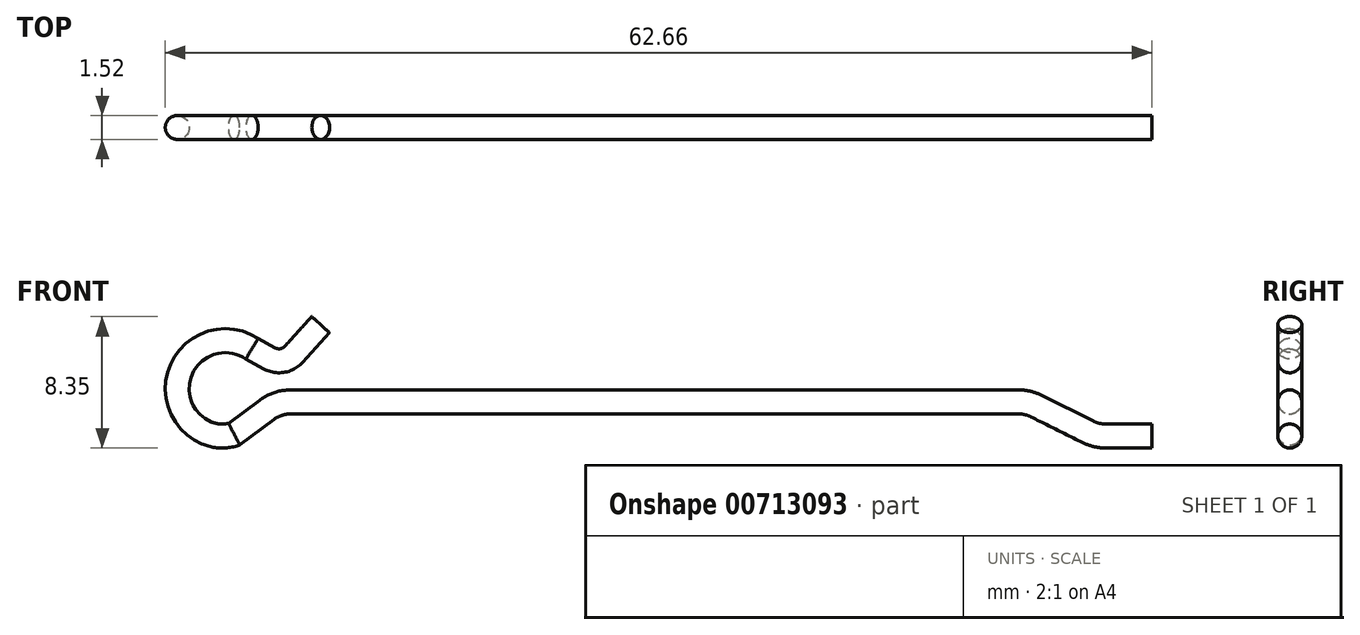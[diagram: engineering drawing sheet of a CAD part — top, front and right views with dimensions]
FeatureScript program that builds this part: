
annotation { "Feature Type Name" : "Feature", "Feature Type Description" : "" }
export const myFeature = defineFeature(function(context is Context, id is Id, definition is map)
    precondition{}
    {
        {
            var Q0;
            Q0=qCreatedBy(makeId("Front.planeOp"),FACE);
            var sketch = newSketch(context, id + "F0", { "sketchPlane" : qUnion([Q0])});
            skLineSegment(sketch, "E0", {"start": v(0, 0) * mm, "end": v(-2.93, 0) * mm});
            skLineSegment(sketch, "E1", {"start": v(-7.34, 1.9) * mm, "end": v(-4.07, 0.27) * mm});
            skLineSegment(sketch, "E2", {"start": v(-8.47, 2.17) * mm, "end": v(-54.7, 2.17) * mm});
            skLineSegment(sketch, "E3", {"start": v(-57.16, 5.54) * mm, "end": v(-56.04, 4.93) * mm});
            skPoint(sketch, "E4.visualSharp", {"position": v(-53.6, 2.17) * mm});
            skPoint(sketch, "E5.visualSharp", {"position": v(-7.87, 2.17) * mm});
            skArc(sketch, "E5.filletArc", {"start": v(-7.34, 1.9) * mm, "mid": v(-7.89, 2.1) * mm, "end": v(-8.47, 2.17) * mm});
            skPoint(sketch, "E6.visualSharp", {"position": v(-3.53, 0) * mm});
            skArc(sketch, "E6.filletArc", {"start": v(-4.07, 0.27) * mm, "mid": v(-3.51, 0.07) * mm, "end": v(-2.93, 0) * mm});
            skArc(sketch, "E7", {"start": v(-57.16, 5.54) * mm, "mid": v(-61.53, 4.46) * mm, "end": v(-60.04, 0.2) * mm});
            skPoint(sketch, "E8", {"position": v(-61.9, 3) * mm});
            skLineSegment(sketch, "E9", {"start": v(-59.64, 2.13) * mm, "end": v(-57.16, 5.54) * mm, "construction": true});
            skPoint(sketch, "E10.visualSharp", {"position": v(-58.16, 0.04) * mm});
            skArc(sketch, "E10.filletArc", {"start": v(-60.04, 0.2) * mm, "mid": v(-59.17, 0) * mm, "end": v(-58.28, 0.12) * mm});
            skLineSegment(sketch, "E11", {"start": v(-54.5, 5.2) * mm, "end": v(-52.79, 7.08) * mm});
            skLineSegment(sketch, "E12", {"start": v(-58.28, 0.12) * mm, "end": v(-58.78, 0.78) * mm});
            skLineSegment(sketch, "E13", {"start": v(-56.2, 1.66) * mm, "end": v(-58.28, 0.12) * mm});
            skPoint(sketch, "E14", {"position": v(-59.05, 0) * mm});
            skPoint(sketch, "E15.visualSharp", {"position": v(-55.53, 2.17) * mm});
            skArc(sketch, "E15.filletArc", {"start": v(-54.7, 2.17) * mm, "mid": v(-55.5, 2.04) * mm, "end": v(-56.2, 1.66) * mm});
            skPoint(sketch, "E16.visualSharp", {"position": v(-55.16, 4.46) * mm});
            skArc(sketch, "E16.filletArc", {"start": v(-56.04, 4.93) * mm, "mid": v(-55.22, 4.8) * mm, "end": v(-54.5, 5.2) * mm});
            skLineSegment(sketch, "E17", {"start": v(-54.5, 5.2) * mm, "end": v(-55.65, 7.4) * mm, "construction": true});
            skSolve(sketch);
        }
        {
            var Q0;
            Q0=sQuery(id+"F0.wireOp",VERTEX,"E0.start");
            var Q1;
            Q1=qCreatedBy(makeId("Right.planeOp"),FACE);
            cPlane(context, id + "F1", {"entities" : qUnion([Q0, Q1]), "cplaneType" : CPlaneType.PLANE_POINT, "offset" : 25.4 * mm, "width" : 152.4 * mm, "height" : 152.4 * mm});
        }
        {
            var Q0;
            Q0=qCreatedBy(id+"F1.planeOp",FACE);
            var sketch = newSketch(context, id + "F2", { "sketchPlane" : qUnion([Q0])});
            skCircle(sketch, "E18", {"center": v(0, 0) * mm, "radius": 0.76 * mm});
            skSolve(sketch);
        }
        {
            var Q0;
            Q0=makeQuery(id+"F2.imprint","IMPRINT",FACE,{"disambiguationData":[TD([[makeQuery(id+"F2.imprint","IMPRINT",EDGE,{"derivedFrom":sQuery(id+"F2.wireOp",EDGE,"E18")}),1.0]])]});
            var Q1;
            Q1=sQuery(id+"F0.wireOp",EDGE,"E0");
            var Q2;
            Q2=sQuery(id+"F0.wireOp",EDGE,"E6.filletArc");
            var Q3;
            Q3=sQuery(id+"F0.wireOp",EDGE,"E1");
            var Q4;
            Q4=sQuery(id+"F0.wireOp",EDGE,"E5.filletArc");
            var Q5;
            Q5=sQuery(id+"F0.wireOp",EDGE,"E2");
            var Q6;
            Q6=sQuery(id+"F0.wireOp",EDGE,"E15.filletArc");
            var Q7;
            Q7=sQuery(id+"F0.wireOp",EDGE,"E16.filletArc");
            var Q8;
            Q8=sQuery(id+"F0.wireOp",EDGE,"E11");
            var Q9;
            Q9=sQuery(id+"F0.wireOp",EDGE,"E3");
            var Q10;
            Q10=sQuery(id+"F0.wireOp",EDGE,"E7");
            var Q11;
            Q11=sQuery(id+"F0.wireOp",EDGE,"E10.filletArc");
            var Q12;
            Q12=sQuery(id+"F0.wireOp",EDGE,"E13");
            sweep(context, id + "F3", {"profiles" : qUnion([Q0]), "path" : qUnion([Q1, Q2, Q3, Q4, Q5, Q6, Q7, Q8, Q9, Q10, Q11, Q12])});
        }
    });
